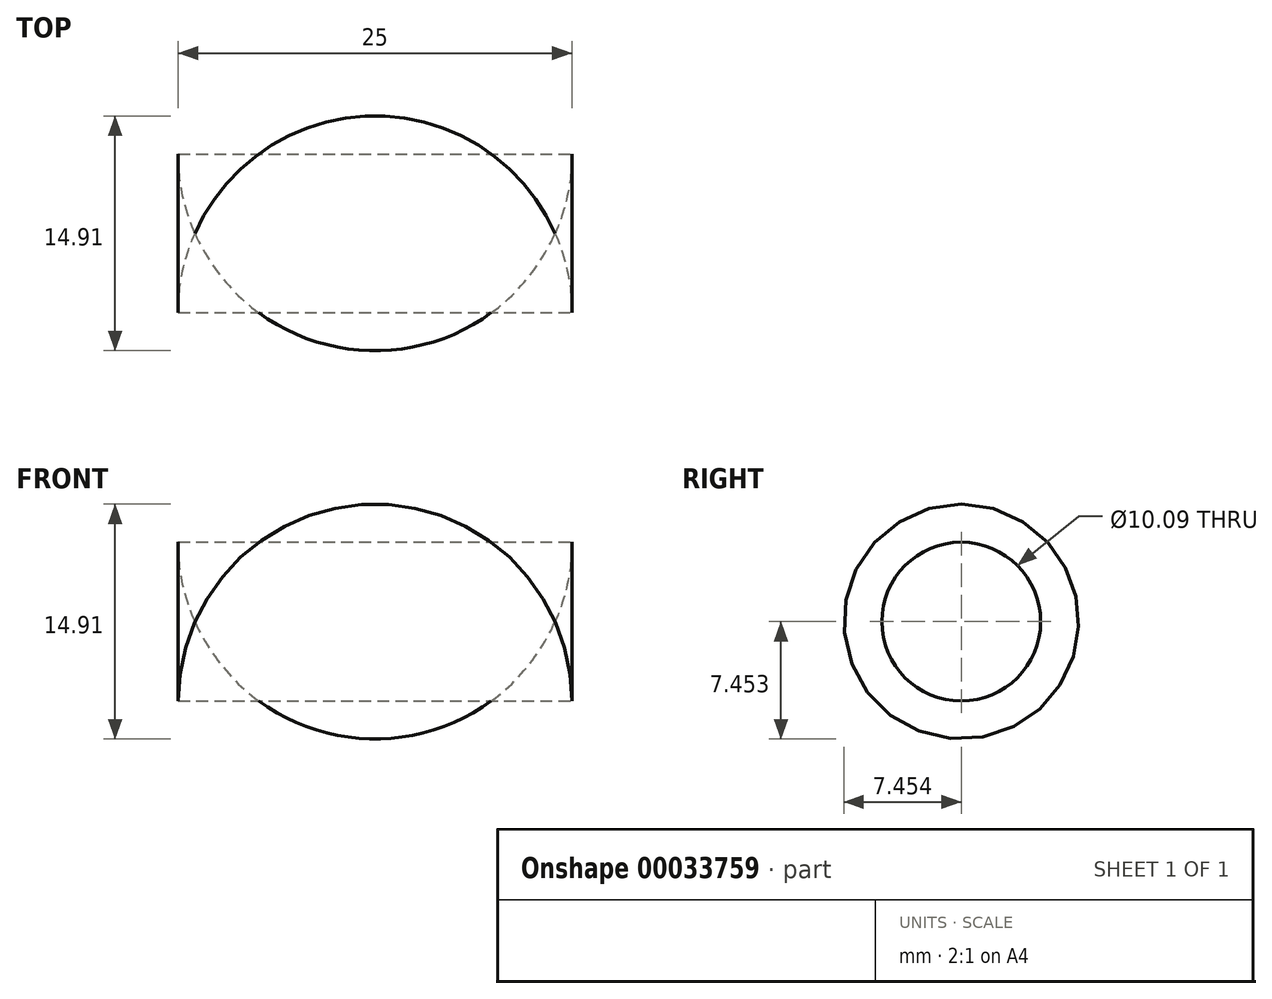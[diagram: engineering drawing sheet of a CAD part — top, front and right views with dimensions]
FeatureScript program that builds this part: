
annotation { "Feature Type Name" : "Feature", "Feature Type Description" : "" }
export const myFeature = defineFeature(function(context is Context, id is Id, definition is map)
    precondition{}
    {
        {
            var Q0;
            Q0=qCreatedBy(makeId("Right.planeOp"),FACE);
            var sketch = newSketch(context, id + "F0", { "sketchPlane" : qUnion([Q0])});
            skCircle(sketch, "E0", {"center": v(-25.82, -30.28) * mm, "radius": 17.54 * mm});
            skSolve(sketch);
        }
        {
            var Q0;
            Q0 = qSketchRegion(id + "F0", true);
            extrude(context, id + "F1", {"entities" : qUnion([Q0]), "depth" : 25 * mm});
        }
        {
            var Q0;
            Q0=makeQuery(id+"F1.opExtrude","CAP_FACE",FACE,{"disambiguationData":[OSD([sQuery(id+"F0.wireOp",EDGE,"E0")])],"isStart":false});
            fillet(context, id + "F2", {"entities" : qUnion([Q0]), "radius" : 12.5 * mm, "tangentPropagation" : true, "allowEdgeOverflow" : false});
        }
        {
            var Q0;
            Q0=makeQuery(id+"F1.opExtrude","CAP_FACE",FACE,{"disambiguationData":[OSD([sQuery(id+"F0.wireOp",EDGE,"E0")])],"isStart":true});
            fillet(context, id + "F3", {"entities" : qUnion([Q0]), "radius" : 12.5 * mm, "tangentPropagation" : true, "allowEdgeOverflow" : false});
        }
        {
            var Q0;
            Q0=makeQuery(id+"F1.opExtrude","CAP_FACE",FACE,{"disambiguationData":[OSD([sQuery(id+"F0.wireOp",EDGE,"E0")])],"isStart":false});
            extrude(context, id + "F4", {"entities" : qUnion([Q0]), "operationType" : NewBodyOperationType.REMOVE, "endBound" : BoundingType.THROUGH_ALL, "oppositeDirection" : true, "depth" : 25.4 * mm});
        }
    });
